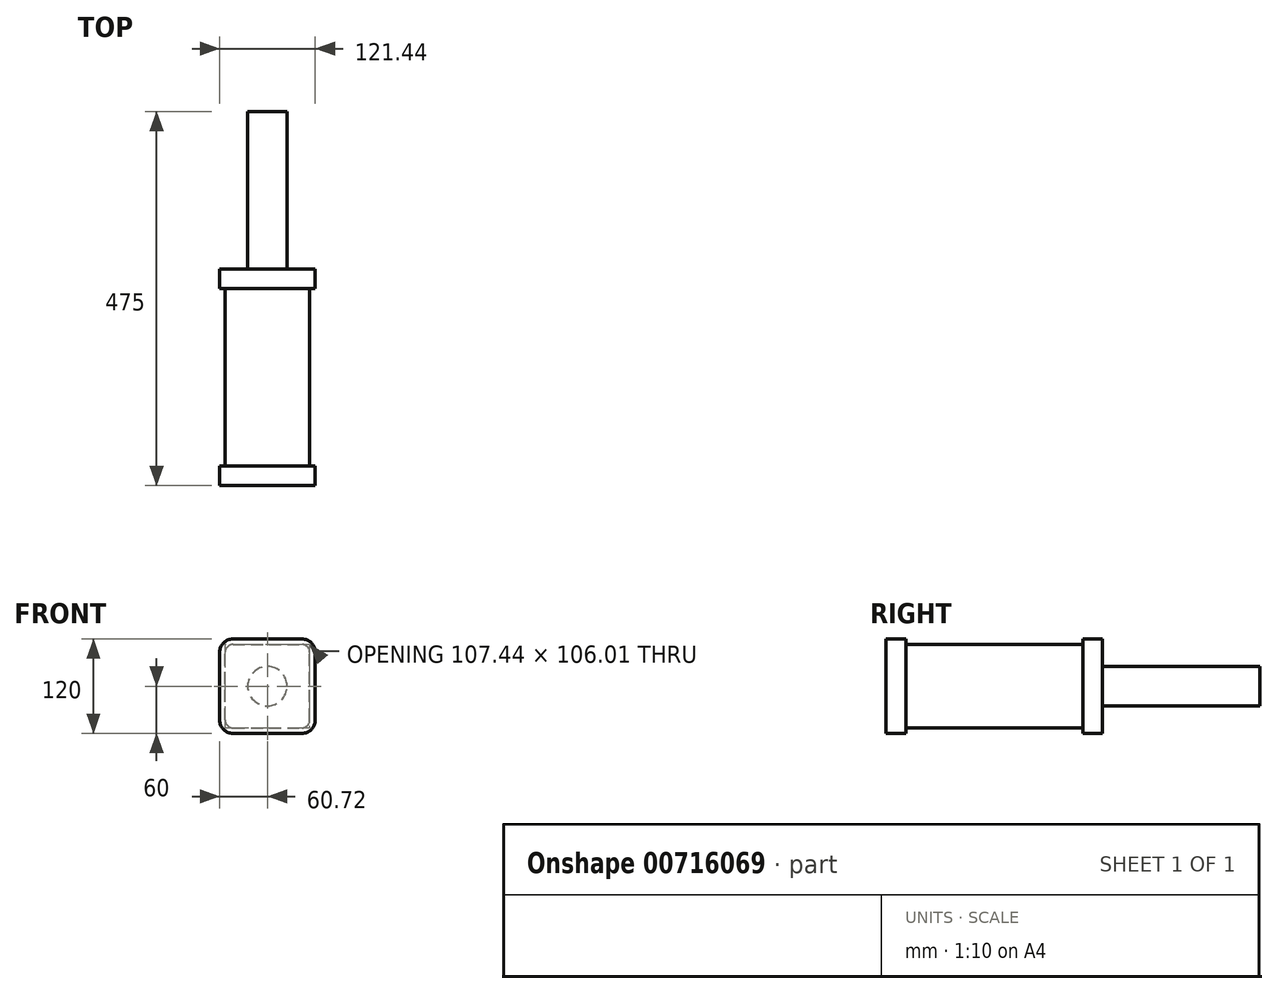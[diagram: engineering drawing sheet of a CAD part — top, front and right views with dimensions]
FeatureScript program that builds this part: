
annotation { "Feature Type Name" : "Feature", "Feature Type Description" : "" }
export const myFeature = defineFeature(function(context is Context, id is Id, definition is map)
    precondition{}
    {
        {
            var Q0;
            Q0=qCreatedBy(makeId("Front.planeOp"),FACE);
            var sketch = newSketch(context, id + "F0", { "sketchPlane" : qUnion([Q0])});
            skLineSegment(sketch, "E0.bottom", {"start": v(43.72, 53) * mm, "end": v(-43.72, 53) * mm});
            skLineSegment(sketch, "E0.top", {"start": v(43.72, -53) * mm, "end": v(-43.72, -53) * mm});
            skLineSegment(sketch, "E0.left", {"start": v(53.72, 43) * mm, "end": v(53.72, -43) * mm});
            skLineSegment(sketch, "E0.right", {"start": v(-53.72, 43) * mm, "end": v(-53.72, -43) * mm});
            skPoint(sketch, "E0.middle", {"position": v(0, 0) * mm});
            skPoint(sketch, "E1.visualSharp", {"position": v(-53.72, 53) * mm});
            skArc(sketch, "E1.filletArc", {"start": v(-43.72, 53) * mm, "mid": v(-50.79, 50.08) * mm, "end": v(-53.72, 43) * mm});
            skPoint(sketch, "E2.visualSharp", {"position": v(53.72, 53) * mm});
            skArc(sketch, "E2.filletArc", {"start": v(53.72, 43) * mm, "mid": v(50.79, 50.08) * mm, "end": v(43.72, 53) * mm});
            skPoint(sketch, "E3.visualSharp", {"position": v(53.72, -53) * mm});
            skArc(sketch, "E3.filletArc", {"start": v(43.72, -53) * mm, "mid": v(50.79, -50.08) * mm, "end": v(53.72, -43) * mm});
            skPoint(sketch, "E4.visualSharp", {"position": v(-53.72, -53) * mm});
            skArc(sketch, "E4.filletArc", {"start": v(-53.72, -43) * mm, "mid": v(-50.79, -50.08) * mm, "end": v(-43.72, -53) * mm});
            skSolve(sketch);
        }
        {
            var Q0;
            Q0 = qSketchRegion(id + "F0", true);
            extrude(context, id + "F1", {"entities" : qUnion([Q0]), "depth" : 250 * mm, "offsetDistance" : 25 * mm});
        }
        {
            var Q0;
            Q0=makeQuery(id+"F1.opExtrude","CAP_FACE",FACE,{"disambiguationData":[OSD([sQuery(id+"F0.wireOp",EDGE,"E0.bottom"),sQuery(id+"F0.wireOp",EDGE,"E0.top"),sQuery(id+"F0.wireOp",EDGE,"E0.left"),sQuery(id+"F0.wireOp",EDGE,"E0.right"),sQuery(id+"F0.wireOp",EDGE,"E1.filletArc"),sQuery(id+"F0.wireOp",EDGE,"E2.filletArc"),sQuery(id+"F0.wireOp",EDGE,"E3.filletArc"),sQuery(id+"F0.wireOp",EDGE,"E4.filletArc")])],"isStart":false});
            var sketch = newSketch(context, id + "F2", { "sketchPlane" : qUnion([Q0])});
            skArc(sketch, "E5.0", {"start": v(-60.72, -43) * mm, "mid": v(-55.74, -55.03) * mm, "end": v(-43.72, -60) * mm});
            skLineSegment(sketch, "E5.1", {"start": v(-60.72, 43) * mm, "end": v(-60.72, -43) * mm});
            skLineSegment(sketch, "E5.2", {"start": v(-43.72, -60) * mm, "end": v(43.72, -60) * mm});
            skArc(sketch, "E5.3", {"start": v(-43.72, 60) * mm, "mid": v(-55.74, 55.03) * mm, "end": v(-60.72, 43) * mm});
            skArc(sketch, "E5.4", {"start": v(43.72, -60) * mm, "mid": v(55.74, -55.03) * mm, "end": v(60.72, -43) * mm});
            skLineSegment(sketch, "E5.5", {"start": v(60.72, -43) * mm, "end": v(60.72, 43) * mm});
            skArc(sketch, "E5.6", {"start": v(60.72, 43) * mm, "mid": v(55.74, 55.03) * mm, "end": v(43.72, 60) * mm});
            skLineSegment(sketch, "E5.7", {"start": v(43.72, 60) * mm, "end": v(-43.72, 60) * mm});
            skSolve(sketch);
        }
        {
            var Q0;
            Q0=makeQuery(id+"F1.opExtrude","CAP_FACE",FACE,{"disambiguationData":[OSD([sQuery(id+"F0.wireOp",EDGE,"E0.bottom"),sQuery(id+"F0.wireOp",EDGE,"E0.top"),sQuery(id+"F0.wireOp",EDGE,"E0.left"),sQuery(id+"F0.wireOp",EDGE,"E0.right"),sQuery(id+"F0.wireOp",EDGE,"E1.filletArc"),sQuery(id+"F0.wireOp",EDGE,"E2.filletArc"),sQuery(id+"F0.wireOp",EDGE,"E3.filletArc"),sQuery(id+"F0.wireOp",EDGE,"E4.filletArc")])],"isStart":true});
            var sketch = newSketch(context, id + "F3", { "sketchPlane" : qUnion([Q0])});
            skArc(sketch, "E6.0", {"start": v(-60.72, -43) * mm, "mid": v(-55.74, -55.03) * mm, "end": v(-43.72, -60) * mm});
            skLineSegment(sketch, "E6.1", {"start": v(-60.72, 43) * mm, "end": v(-60.72, -43) * mm});
            skLineSegment(sketch, "E6.2", {"start": v(-43.72, -60) * mm, "end": v(43.72, -60) * mm});
            skArc(sketch, "E6.3", {"start": v(-43.72, 60) * mm, "mid": v(-55.74, 55.03) * mm, "end": v(-60.72, 43) * mm});
            skArc(sketch, "E6.4", {"start": v(43.72, -60) * mm, "mid": v(55.74, -55.03) * mm, "end": v(60.72, -43) * mm});
            skLineSegment(sketch, "E6.5", {"start": v(60.72, -43) * mm, "end": v(60.72, 43) * mm});
            skArc(sketch, "E6.6", {"start": v(60.72, 43) * mm, "mid": v(55.74, 55.03) * mm, "end": v(43.72, 60) * mm});
            skLineSegment(sketch, "E6.7", {"start": v(43.72, 60) * mm, "end": v(-43.72, 60) * mm});
            skSolve(sketch);
        }
        {
            var Q0;
            Q0 = qSketchRegion(id + "F2", true);
            var Q1;
            Q1 = qSketchRegion(id + "F3", true);
            extrude(context, id + "F4", {"entities" : qUnion([Q0, Q1]), "operationType" : NewBodyOperationType.ADD, "depth" : 25 * mm, "offsetDistance" : 25 * mm});
        }
        {
            var Q0;
            Q0=makeQuery(id+"F4.boolean.opBoolean","MERGE",FACE,{"derivedFrom":[makeQuery(id+"F1.opExtrude","CAP_FACE",FACE,{"disambiguationData":[OSD([sQuery(id+"F0.wireOp",EDGE,"E0.bottom"),sQuery(id+"F0.wireOp",EDGE,"E0.top"),sQuery(id+"F0.wireOp",EDGE,"E0.left"),sQuery(id+"F0.wireOp",EDGE,"E0.right"),sQuery(id+"F0.wireOp",EDGE,"E1.filletArc"),sQuery(id+"F0.wireOp",EDGE,"E2.filletArc"),sQuery(id+"F0.wireOp",EDGE,"E3.filletArc"),sQuery(id+"F0.wireOp",EDGE,"E4.filletArc")])],"isStart":true}),makeQuery(id+"F4.opExtrude","CAP_FACE",FACE,{"disambiguationData":[OSD([sQuery(id+"F3.wireOp",EDGE,"E6.0"),sQuery(id+"F3.wireOp",EDGE,"E6.1"),sQuery(id+"F3.wireOp",EDGE,"E6.2"),sQuery(id+"F3.wireOp",EDGE,"E6.3"),sQuery(id+"F3.wireOp",EDGE,"E6.4"),sQuery(id+"F3.wireOp",EDGE,"E6.5"),sQuery(id+"F3.wireOp",EDGE,"E6.6"),sQuery(id+"F3.wireOp",EDGE,"E6.7")])],"isStart":true})]});
            var sketch = newSketch(context, id + "F5", { "sketchPlane" : qUnion([Q0])});
            skCircle(sketch, "E7", {"center": v(0, 0) * mm, "radius": 25.05 * mm});
            skSolve(sketch);
        }
        {
            var Q0;
            Q0=makeQuery(id+"F5.imprint","IMPRINT",FACE,{"disambiguationData":[TD([[makeQuery(id+"F5.imprint","IMPRINT",EDGE,{"derivedFrom":sQuery(id+"F5.wireOp",EDGE,"E7")}),1.0]])]});
            extrude(context, id + "F6", {"entities" : qUnion([Q0]), "operationType" : NewBodyOperationType.ADD, "depth" : 200 * mm, "offsetDistance" : 25 * mm});
        }
    });
